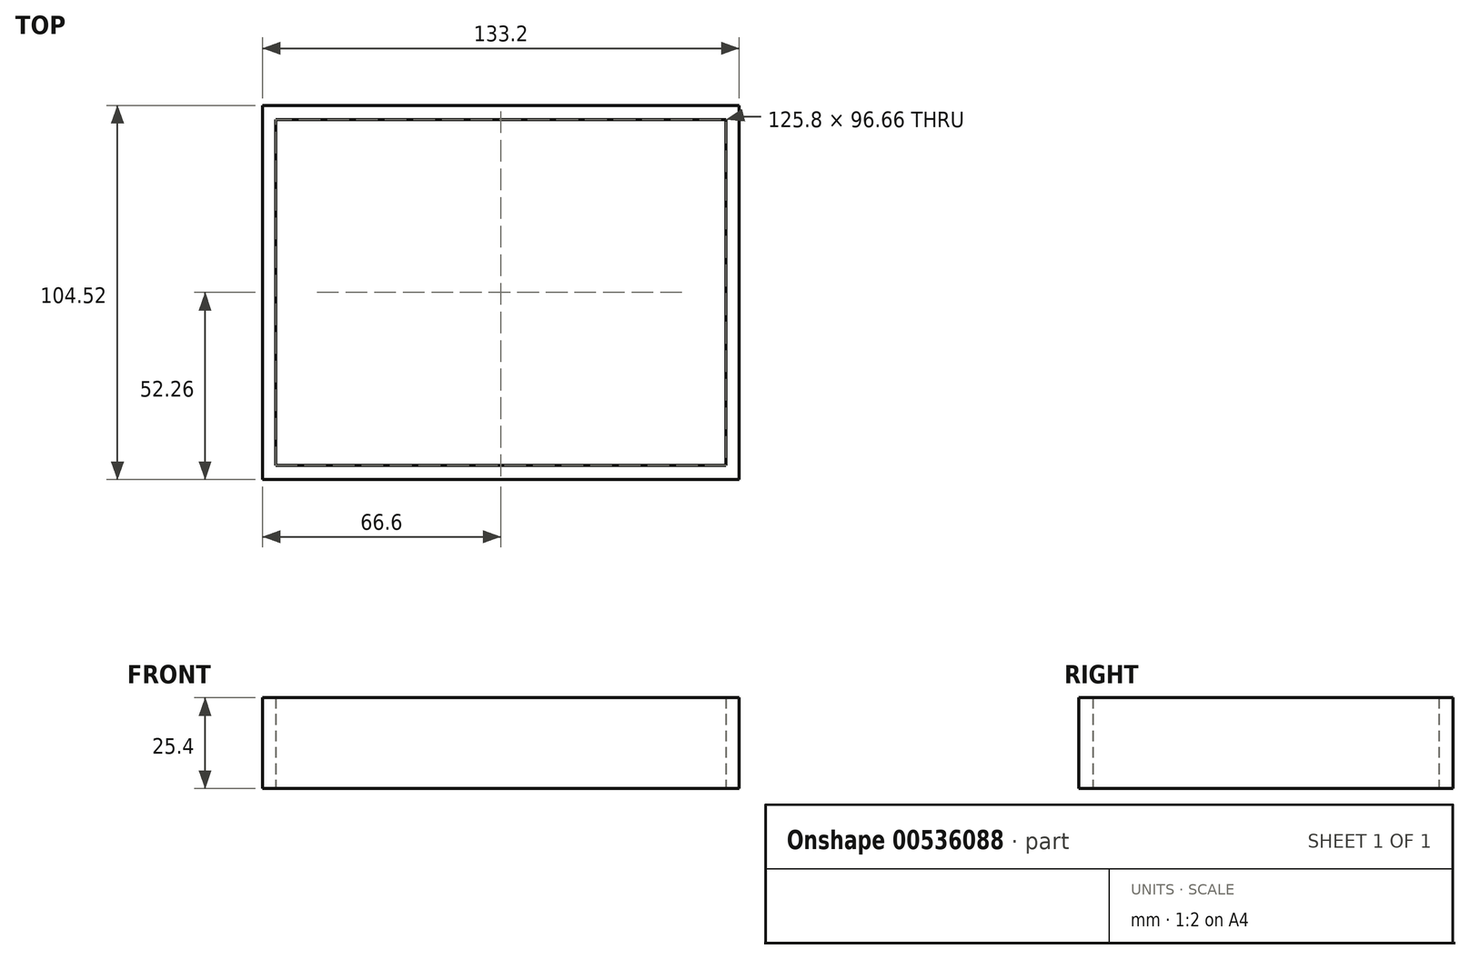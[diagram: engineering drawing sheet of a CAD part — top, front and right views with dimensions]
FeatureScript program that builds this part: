
annotation { "Feature Type Name" : "Feature", "Feature Type Description" : "" }
export const myFeature = defineFeature(function(context is Context, id is Id, definition is map)
    precondition{}
    {
        {
            var Q0;
            Q0=qCreatedBy(makeId("Top.planeOp"),FACE);
            var sketch = newSketch(context, id + "F0", { "sketchPlane" : qUnion([Q0])});
            skLineSegment(sketch, "E0.bottom", {"start": v(-62.9, 48.33) * mm, "end": v(62.9, 48.33) * mm});
            skLineSegment(sketch, "E0.top", {"start": v(-62.9, -48.33) * mm, "end": v(62.9, -48.33) * mm});
            skLineSegment(sketch, "E0.left", {"start": v(-62.9, 48.33) * mm, "end": v(-62.9, -48.33) * mm});
            skLineSegment(sketch, "E0.right", {"start": v(62.9, 48.33) * mm, "end": v(62.9, -48.33) * mm});
            skPoint(sketch, "E0.middle", {"position": v(0, 0) * mm});
            skLineSegment(sketch, "E1.bottom", {"start": v(66.6, 52.26) * mm, "end": v(-66.6, 52.26) * mm});
            skLineSegment(sketch, "E1.top", {"start": v(66.6, -52.26) * mm, "end": v(-66.6, -52.26) * mm});
            skLineSegment(sketch, "E1.left", {"start": v(66.6, 52.26) * mm, "end": v(66.6, -52.26) * mm});
            skLineSegment(sketch, "E1.right", {"start": v(-66.6, 52.26) * mm, "end": v(-66.6, -52.26) * mm});
            skLineSegment(sketch, "E2.bottom", {"start": v(-62.9, 48.33) * mm, "end": v(-37.46, 48.33) * mm});
            skLineSegment(sketch, "E2.top", {"start": v(-62.9, -7.17) * mm, "end": v(-37.46, -7.17) * mm});
            skLineSegment(sketch, "E2.left", {"start": v(-62.9, 48.33) * mm, "end": v(-62.9, -7.17) * mm});
            skLineSegment(sketch, "E2.right", {"start": v(-37.46, 48.33) * mm, "end": v(-37.46, -7.17) * mm});
            skLineSegment(sketch, "E3.bottom", {"start": v(62.9, 48.33) * mm, "end": v(2.31, 48.33) * mm});
            skLineSegment(sketch, "E3.top", {"start": v(62.9, 26.82) * mm, "end": v(2.31, 26.82) * mm});
            skLineSegment(sketch, "E3.left", {"start": v(62.9, 48.33) * mm, "end": v(62.9, 26.82) * mm});
            skLineSegment(sketch, "E3.right", {"start": v(2.31, 48.33) * mm, "end": v(2.31, 26.82) * mm});
            skLineSegment(sketch, "E4.bottom", {"start": v(-62.9, 48.33) * mm, "end": v(-34.46, 48.33) * mm});
            skLineSegment(sketch, "E4.top", {"start": v(-62.9, -9.25) * mm, "end": v(-34.46, -9.25) * mm});
            skLineSegment(sketch, "E4.left", {"start": v(-62.9, 48.33) * mm, "end": v(-62.9, -9.25) * mm});
            skLineSegment(sketch, "E4.right", {"start": v(-34.46, 48.33) * mm, "end": v(-34.46, -9.25) * mm});
            skSolve(sketch);
        }
        {
            var Q0;
            {var subQ0=sQuery(id+"F0.wireOp",EDGE,"E0.bottom");Q0=makeQuery(id+"F0.imprint","IMPRINT",FACE,{"disambiguationData":[TD([[makeQuery(id+"F0.imprint","IMPRINT",EDGE,{"derivedFrom":subQ0}),1.0]])]});}
            extrude(context, id + "F1", {"entities" : qUnion([Q0]), "depth" : 25.4 * mm, "offsetDistance" : 25.4 * mm});
        }
    });
